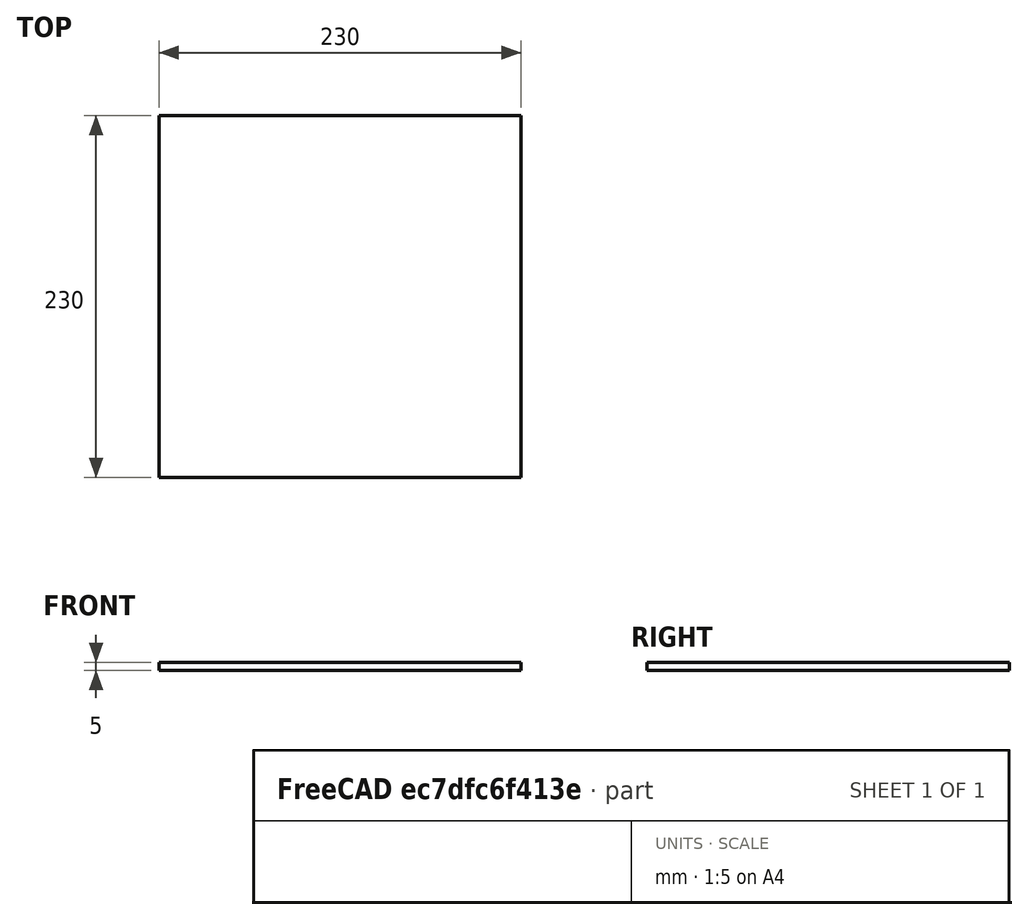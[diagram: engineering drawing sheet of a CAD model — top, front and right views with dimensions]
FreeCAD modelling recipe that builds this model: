
FCSTD DOCUMENT  (FreeCAD 0.21R33668 +7 (Git))
Label: Table
License: All rights reserved
LicenseURL: https://en.wikipedia.org/wiki/All_rights_reserved
objects: Sketcher::SketchObject×1, PartDesign::Pad×1, PartDesign::Body×1
note: 4 computed .brp shape members not serialized (recipe doc carries the construction recipe); baked Part::Feature solids carry a one-line shape summary decoded from their .brp

FEATURE [Sketcher::SketchObject] Sketch
  FullyConstrained = true
  MapMode = 5
  Support = -> [XY_Plane]
  sketch-geometry (4):
    g0: LineSegment StartX=-115 StartY=-115 StartZ=0 EndX=115 EndY=-115 EndZ=0
    g1: LineSegment StartX=115 StartY=-115 StartZ=0 EndX=115 EndY=115 EndZ=0
    g2: LineSegment StartX=115 StartY=115 StartZ=0 EndX=-115 EndY=115 EndZ=0
    g3: LineSegment StartX=-115 StartY=115 StartZ=0 EndX=-115 EndY=-115 EndZ=0
  constraints (11):
    c: Coincident(g0,g1)
    c: Coincident(g1,g2)
    c: Coincident(g2,g3)
    c: Coincident(g3,g0)
    c: Horizontal(g0)
    c: Horizontal(g2)
    c: Vertical(g1)
    c: Vertical(g3)
    c: Symmetric(g1,g0,g-1)
    c: DistanceX(g2,g2) = 230
    c: DistanceY(g1,g1) = 230
FEATURE [PartDesign::Pad] Pad
  Direction = (0,0,1)
  Length = 5
  Length2 = 10
  Profile = -> Sketch
  ReferenceAxis = -> Sketch [N_Axis]
  Type = 0
FEATURE [PartDesign::Body] Body
  Group = -> [Sketch,Pad]
  Origin = -> Origin
  Tip = -> Pad
